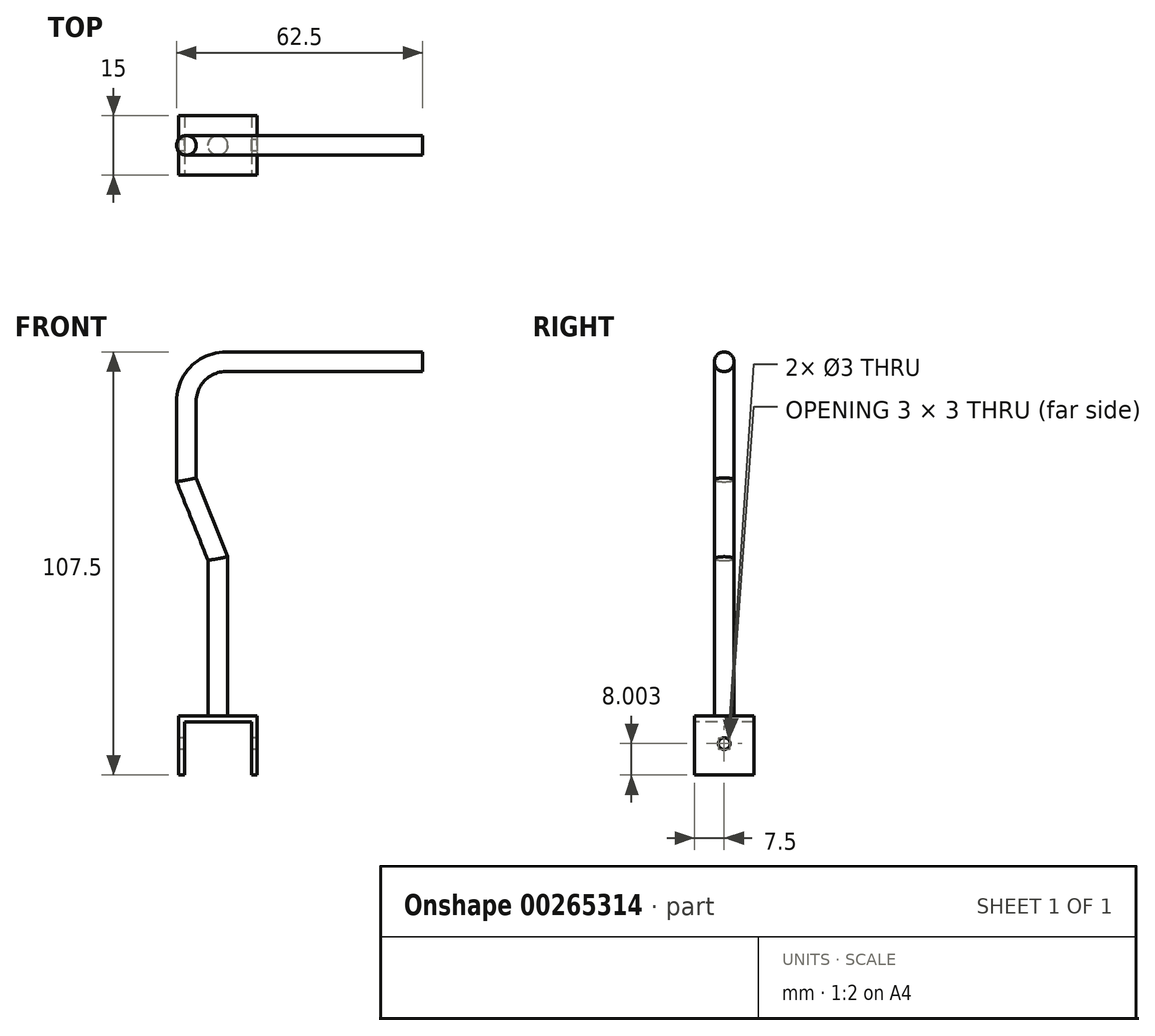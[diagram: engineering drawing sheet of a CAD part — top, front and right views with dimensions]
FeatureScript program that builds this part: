
annotation { "Feature Type Name" : "Feature", "Feature Type Description" : "" }
export const myFeature = defineFeature(function(context is Context, id is Id, definition is map)
    precondition{}
    {
        {
            var Q0;
            Q0=qCreatedBy(makeId("Front.planeOp"),FACE);
            var sketch = newSketch(context, id + "F0", { "sketchPlane" : qUnion([Q0])});
            skLineSegment(sketch, "E0", {"start": v(0, 39.54) * mm, "end": v(-50, 39.54) * mm});
            skLineSegment(sketch, "E1", {"start": v(-60, 29.54) * mm, "end": v(-60, 9.54) * mm});
            skPoint(sketch, "E2.visualSharp", {"position": v(-60, 39.54) * mm});
            skArc(sketch, "E2.filletArc", {"start": v(-50, 39.54) * mm, "mid": v(-57.07, 36.61) * mm, "end": v(-60, 29.54) * mm});
            skLineSegment(sketch, "E3", {"start": v(-60, 9.54) * mm, "end": v(-52, -10.46) * mm});
            skLineSegment(sketch, "E4", {"start": v(-52, -10.46) * mm, "end": v(-52, -50.46) * mm});
            skSolve(sketch);
        }
        {
            var Q0;
            Q0=qCreatedBy(makeId("Right.planeOp"),FACE);
            var sketch = newSketch(context, id + "F1", { "sketchPlane" : qUnion([Q0])});
            skCircle(sketch, "E5", {"center": v(0, 39.54) * mm, "radius": 2.5 * mm});
            skSolve(sketch);
        }
        {
            var Q0;
            Q0=makeQuery(id+"F1.imprint","IMPRINT",FACE,{"disambiguationData":[TD([[makeQuery(id+"F1.imprint","IMPRINT",EDGE,{"derivedFrom":sQuery(id+"F1.wireOp",EDGE,"E5")}),1.0]])]});
            var Q1;
            Q1 = qConstructionFilter(qBodyType(qCreatedBy(id + "F0" ,EDGE), BodyType.WIRE), ConstructionObject.NO);
            sweep(context, id + "F2", {"profiles" : qUnion([Q0]), "path" : qUnion([Q1])});
        }
        {
            var Q0;
            Q0=qCreatedBy(makeId("Right.planeOp"),FACE);
            cPlane(context, id + "F3", {"entities" : qUnion([Q0]), "cplaneType" : CPlaneType.OFFSET, "offset" : (60 - 8) * mm, "oppositeDirection" : true, "width" : 150 * mm, "height" : 150 * mm});
        }
        {
            var Q0;
            Q0=qCreatedBy(id+"F3.planeOp",FACE);
            var sketch = newSketch(context, id + "F4", { "sketchPlane" : qUnion([Q0])});
            skLineSegment(sketch, "E6.bottom", {"start": v(7.5, -50.46) * mm, "end": v(-7.5, -50.46) * mm});
            skLineSegment(sketch, "E6.top", {"start": v(7.5, -65.46) * mm, "end": v(-7.5, -65.46) * mm});
            skLineSegment(sketch, "E6.left", {"start": v(7.5, -50.46) * mm, "end": v(7.5, -65.46) * mm});
            skLineSegment(sketch, "E6.right", {"start": v(-7.5, -50.46) * mm, "end": v(-7.5, -65.46) * mm});
            skSolve(sketch);
        }
        {
            var Q0;
            Q0=makeQuery(id+"F4.imprint","IMPRINT",FACE,{"disambiguationData":[TD([[makeQuery(id+"F4.imprint","IMPRINT",EDGE,{"derivedFrom":sQuery(id+"F4.wireOp",EDGE,"E6.bottom")}),1.0]])]});
            extrude(context, id + "F5", {"entities" : qUnion([Q0]), "operationType" : NewBodyOperationType.ADD, "endBound" : BoundingType.SYMMETRIC, "depth" : 20 * mm});
        }
        {
            var Q0;
            Q0=makeQuery(id+"F5.opExtrude","SWEPT_FACE",FACE,{"disambiguationData":[OSD([sQuery(id+"F4.wireOp",EDGE,"E6.right")])]});
            var sketch = newSketch(context, id + "F6", { "sketchPlane" : qUnion([Q0])});
            skLineSegment(sketch, "E7.0", {"start": v(-60.5, -68.96) * mm, "end": v(-60.5, -51.96) * mm});
            skLineSegment(sketch, "E7.2", {"start": v(-43.5, -51.96) * mm, "end": v(-43.5, -68.96) * mm});
            skLineSegment(sketch, "E7.3", {"start": v(-60.5, -51.96) * mm, "end": v(-43.5, -51.96) * mm});
            skLineSegment(sketch, "E8", {"start": v(-60.5, -65.46) * mm, "end": v(-60.5, -68.96) * mm});
            skLineSegment(sketch, "E9", {"start": v(-60.5, -65.46) * mm, "end": v(-43.5, -65.46) * mm});
            skLineSegment(sketch, "E10", {"start": v(-43.5, -68.96) * mm, "end": v(-43.5, -65.46) * mm});
            skSolve(sketch);
        }
        {
            var Q0;
            Q0 = qSketchRegion(id + "F6", true);
            extrude(context, id + "F7", {"entities" : qUnion([Q0]), "operationType" : NewBodyOperationType.REMOVE, "oppositeDirection" : true, "depth" : 25 * mm});
        }
        {
            var Q0;
            Q0=makeQuery(id+"F5.opExtrude","CAP_FACE",FACE,{"disambiguationData":[OSD([sQuery(id+"F4.wireOp",EDGE,"E6.bottom"),sQuery(id+"F4.wireOp",EDGE,"E6.top"),sQuery(id+"F4.wireOp",EDGE,"E6.left"),sQuery(id+"F4.wireOp",EDGE,"E6.right")])],"isStart":true});
            var sketch = newSketch(context, id + "F8", { "sketchPlane" : qUnion([Q0])});
            skCircle(sketch, "E11", {"center": v(0, -57.46) * mm, "radius": 1.5 * mm});
            skSolve(sketch);
        }
        {
            var Q0;
            Q0 = qSketchRegion(id + "F8", true);
            extrude(context, id + "F9", {"entities" : qUnion([Q0]), "operationType" : NewBodyOperationType.REMOVE, "oppositeDirection" : true, "depth" : 25 * mm});
        }
    });
